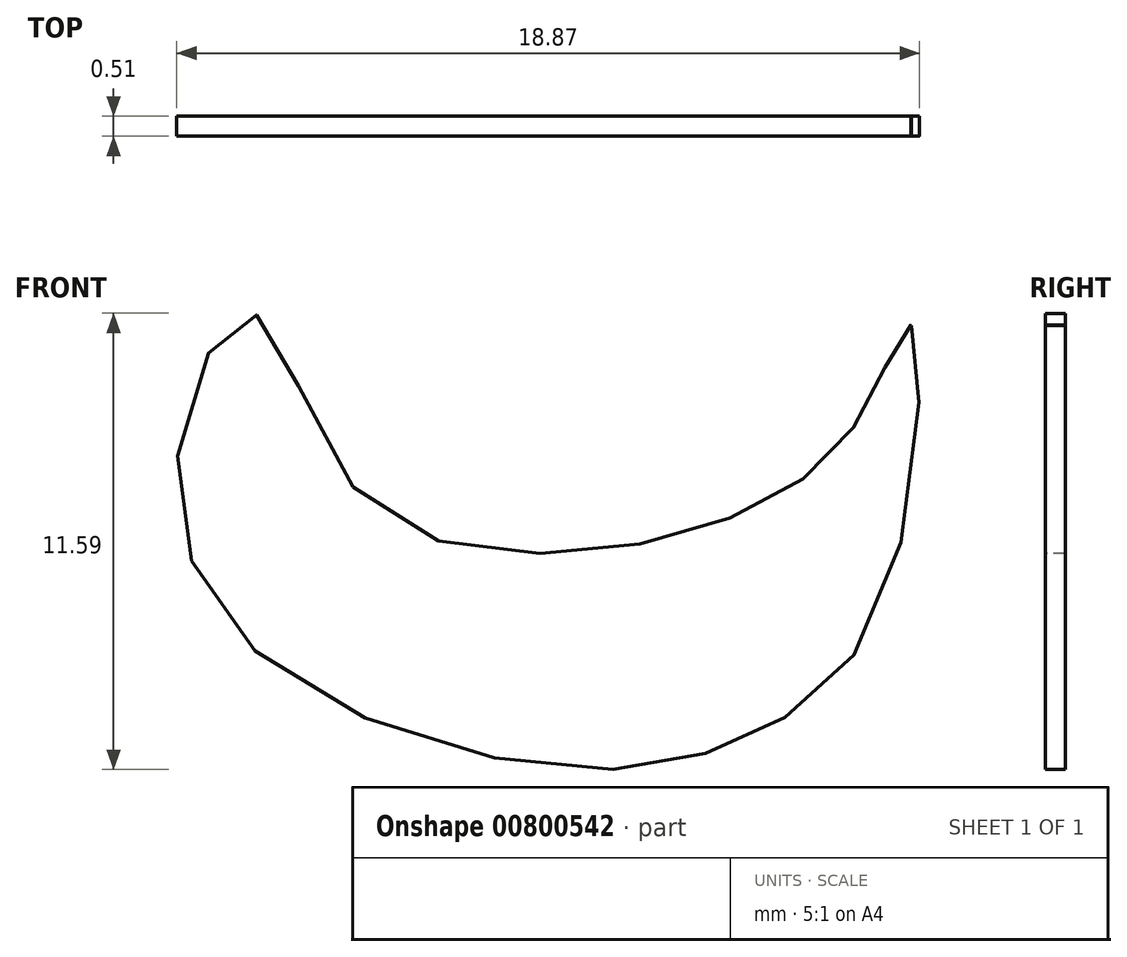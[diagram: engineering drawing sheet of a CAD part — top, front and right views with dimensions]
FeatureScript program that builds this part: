
annotation { "Feature Type Name" : "Feature", "Feature Type Description" : "" }
export const myFeature = defineFeature(function(context is Context, id is Id, definition is map)
    precondition{}
    {
        {
            var Q0;
            Q0=qCreatedBy(makeId("Front.planeOp"),FACE);
            var sketch = newSketch(context, id + "F0", { "sketchPlane" : qUnion([Q0])});
            skFitSpline(sketch, "E0", {"points": [v(-67.99, 55.94) * mm, v(-65.55, 51.68) * mm, v(-60.68, 49.85) * mm, v(-55.81, 50.77) * mm, v(-53.08, 52.6) * mm, v(-51.86, 54.72) * mm, v(-51.25, 55.64) * mm, v(-51.86, 48.94) * mm, v(-55.2, 45.29) * mm, v(-59.77, 44.37) * mm, v(-67.99, 47.42) * mm, v(-69.82, 52.9) * mm, v(-67.99, 55.94) * mm]});
            skFitSpline(sketch, "E1", {"points": [v(-51.25, 55.64) * mm, v(-48.5, 55.94) * mm, v(-47.3, 55.94) * mm, v(-51.25, 55.64) * mm]});
            skFitSpline(sketch, "E2", {"points": [v(-47.3, 55.94) * mm, v(-51.25, 55.64) * mm], "startDerivative": vector(-3.96, -0.3) * mm, "endDerivative": vector(-3.96, -0.3) * mm});
            skSolve(sketch);
        }
        {
            var Q0;
            {var subQ0=sQuery(id+"F0.wireOp",EDGE,"E1");var subQ1=sQuery(id+"F0.wireOp",EDGE,"E0");var subQ3=makeQuery(id+"F0.imprint","INTERSECT",VERTEX,{"derivedFrom":[subQ1,subQ0]});Q0=makeQuery(id+"F0.imprint","IMPRINT",FACE,{"disambiguationData":[TD([[makeQuery(id+"F0.imprint","IMPRINT",EDGE,{"disambiguationData":[TD([[subQ3,1.0]])],"derivedFrom":subQ1}),-1.0]])]});}
            extrude(context, id + "F1", {"entities" : qUnion([Q0]), "oppositeDirection" : true, "depth" : 0.5 * mm, "offsetDistance" : 25.4 * mm});
        }
    });
